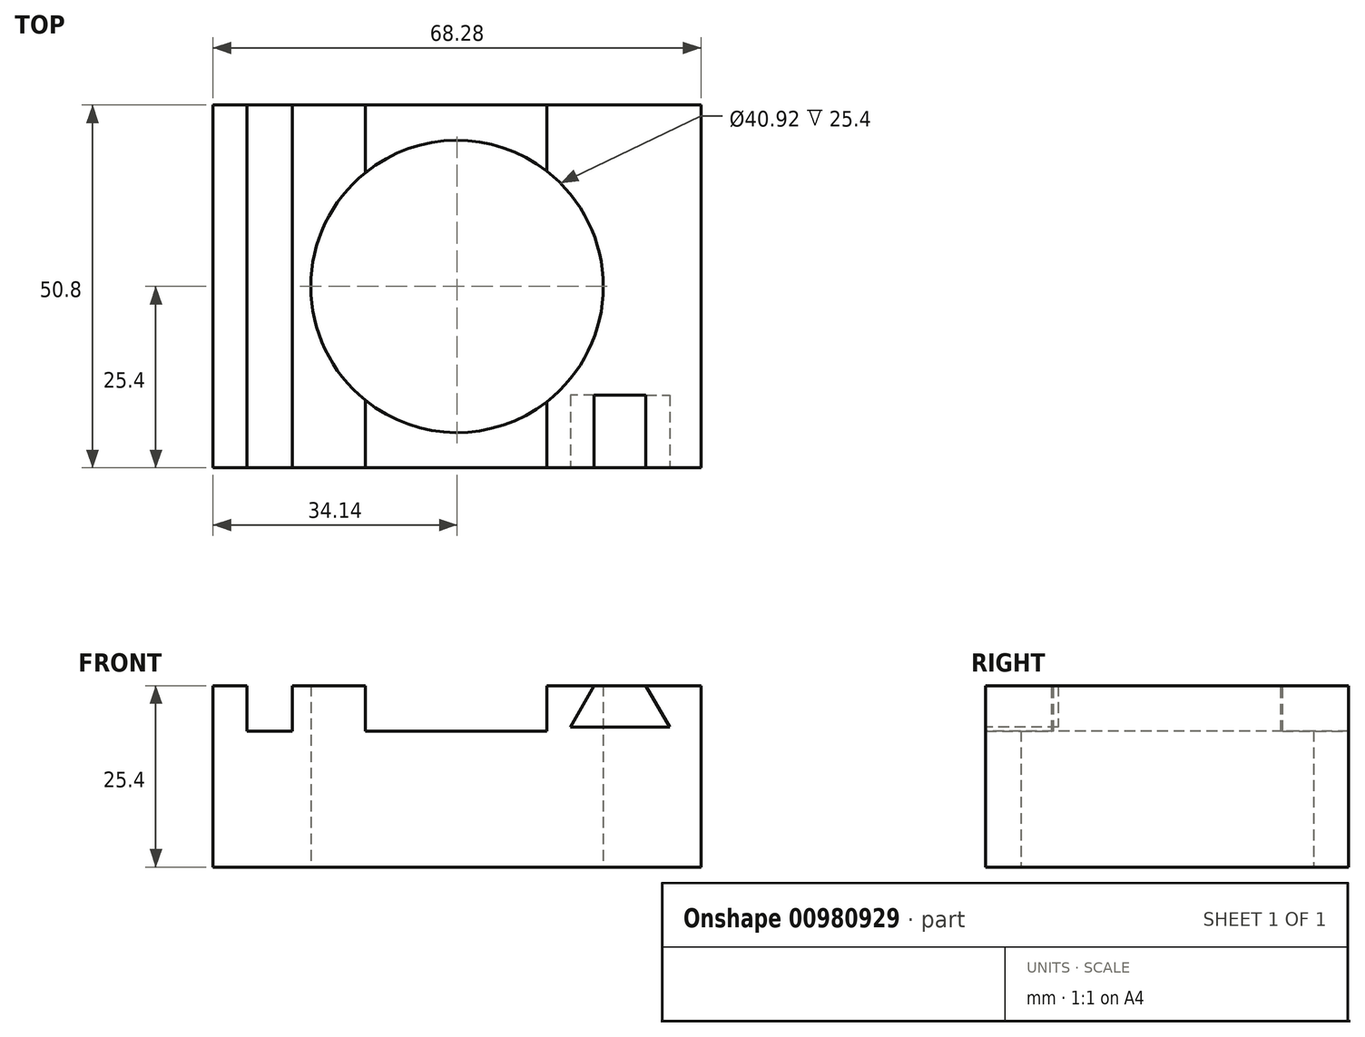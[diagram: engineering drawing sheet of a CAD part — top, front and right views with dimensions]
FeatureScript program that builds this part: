
annotation { "Feature Type Name" : "Feature", "Feature Type Description" : "" }
export const myFeature = defineFeature(function(context is Context, id is Id, definition is map)
    precondition{}
    {
        {
            var Q0;
            Q0=qCreatedBy(makeId("Top.planeOp"),FACE);
            var sketch = newSketch(context, id + "F0", { "sketchPlane" : qUnion([Q0])});
            skLineSegment(sketch, "E0.bottom", {"start": v(34.14, 25.4) * mm, "end": v(-34.14, 25.4) * mm});
            skLineSegment(sketch, "E0.top", {"start": v(34.14, -25.4) * mm, "end": v(-34.14, -25.4) * mm});
            skLineSegment(sketch, "E0.left", {"start": v(34.14, 25.4) * mm, "end": v(34.14, -25.4) * mm});
            skLineSegment(sketch, "E0.right", {"start": v(-34.14, 25.4) * mm, "end": v(-34.14, -25.4) * mm});
            skPoint(sketch, "E0.middle", {"position": v(0, 0) * mm});
            skCircle(sketch, "E1", {"center": v(0, 0) * mm, "radius": 20.46 * mm});
            skSolve(sketch);
        }
        {
            var Q0;
            Q0 = qSketchRegion(id + "F0", true);
            extrude(context, id + "F1", {"entities" : qUnion([Q0]), "depth" : 25.4 * mm, "offsetDistance" : 25.4 * mm});
        }
        {
            var Q0;
            Q0=makeQuery(id+"F1.opExtrude","CAP_FACE",FACE,{"disambiguationData":[OSD([sQuery(id+"F0.wireOp",EDGE,"E0.bottom"),sQuery(id+"F0.wireOp",EDGE,"E0.top"),sQuery(id+"F0.wireOp",EDGE,"E0.left"),sQuery(id+"F0.wireOp",EDGE,"E0.right"),sQuery(id+"F0.wireOp",EDGE,"E1")])],"isStart":false});
            var sketch = newSketch(context, id + "F2", { "sketchPlane" : qUnion([Q0])});
            skLineSegment(sketch, "E2.bottom", {"start": v(-29.42, 25.4) * mm, "end": v(-23.07, 25.4) * mm});
            skLineSegment(sketch, "E2.top", {"start": v(-29.42, -25.4) * mm, "end": v(-23.07, -25.4) * mm});
            skLineSegment(sketch, "E2.left", {"start": v(-29.42, 25.4) * mm, "end": v(-29.42, -25.4) * mm});
            skLineSegment(sketch, "E2.right", {"start": v(-23.07, 25.4) * mm, "end": v(-23.07, -25.4) * mm});
            skLineSegment(sketch, "E3", {"start": v(-12.84, 25.4) * mm, "end": v(-12.84, -25.4) * mm});
            skLineSegment(sketch, "E4", {"start": v(-12.84, -25.4) * mm, "end": v(12.56, -25.4) * mm});
            skLineSegment(sketch, "E5", {"start": v(12.56, -25.4) * mm, "end": v(12.56, 25.4) * mm});
            skLineSegment(sketch, "E6", {"start": v(0, 25.4) * mm, "end": v(-0.14, -25.4) * mm, "construction": true});
            skSolve(sketch);
        }
        {
            var Q0;
            Q0=makeQuery(id+"F2.imprint","IMPRINT",FACE,{"disambiguationData":[TD([[makeQuery(id+"F2.imprint","IMPRINT",EDGE,{"derivedFrom":sQuery(id+"F2.wireOp",EDGE,"E2.bottom")}),1.0]])]});
            var Q1;
            {var subQ0=sQuery(id+"F2.wireOp",EDGE,"E3");var subQ1=makeQuery(id+"F1.opExtrude","CAP_EDGE",EDGE,{"disambiguationData":[OSD([sQuery(id+"F0.wireOp",EDGE,"E0.bottom")])],"isStart":false});var subQ2=makeQuery(id+"F2.imprint","INTERSECT",VERTEX,{"derivedFrom":[subQ1,subQ0]});Q1=makeQuery(id+"F2.imprint","IMPRINT",FACE,{"disambiguationData":[TD([[makeQuery(id+"F2.imprint","IMPRINT",EDGE,{"disambiguationData":[TD([[subQ2,-1.0]])],"derivedFrom":subQ0}),1.0]])]});}
            var Q2;
            {var subQ0=sQuery(id+"F2.wireOp",EDGE,"E4");Q2=makeQuery(id+"F2.imprint","IMPRINT",FACE,{"disambiguationData":[TD([[makeQuery(id+"F2.imprint","IMPRINT",EDGE,{"derivedFrom":subQ0}),-1.0]])]});}
            extrude(context, id + "F3", {"entities" : qUnion([Q0, Q1, Q2]), "operationType" : NewBodyOperationType.REMOVE, "oppositeDirection" : true, "depth" : 6.35 * mm, "offsetDistance" : 25.4 * mm});
        }
        {
            var Q0;
            Q0=makeQuery(id+"F1.opExtrude","SWEPT_FACE",FACE,{"disambiguationData":[OSD([sQuery(id+"F0.wireOp",EDGE,"E0.top")])]});
            var sketch = newSketch(context, id + "F4", { "sketchPlane" : qUnion([Q0])});
            skLineSegment(sketch, "E7", {"start": v(19.19, 25.4) * mm, "end": v(15.84, 19.6) * mm});
            skLineSegment(sketch, "E8", {"start": v(15.84, 19.6) * mm, "end": v(29.75, 19.6) * mm});
            skLineSegment(sketch, "E9", {"start": v(29.75, 19.6) * mm, "end": v(26.4, 25.4) * mm});
            skSolve(sketch);
        }
        {
            var Q0;
            {var subQ0=sQuery(id+"F4.wireOp",EDGE,"E7");Q0=makeQuery(id+"F4.imprint","IMPRINT",FACE,{"disambiguationData":[TD([[makeQuery(id+"F4.imprint","IMPRINT",EDGE,{"derivedFrom":subQ0}),1.0]])]});}
            extrude(context, id + "F5", {"entities" : qUnion([Q0]), "operationType" : NewBodyOperationType.REMOVE, "oppositeDirection" : true, "depth" : 10.16 * mm, "offsetDistance" : 25.4 * mm});
        }
    });
